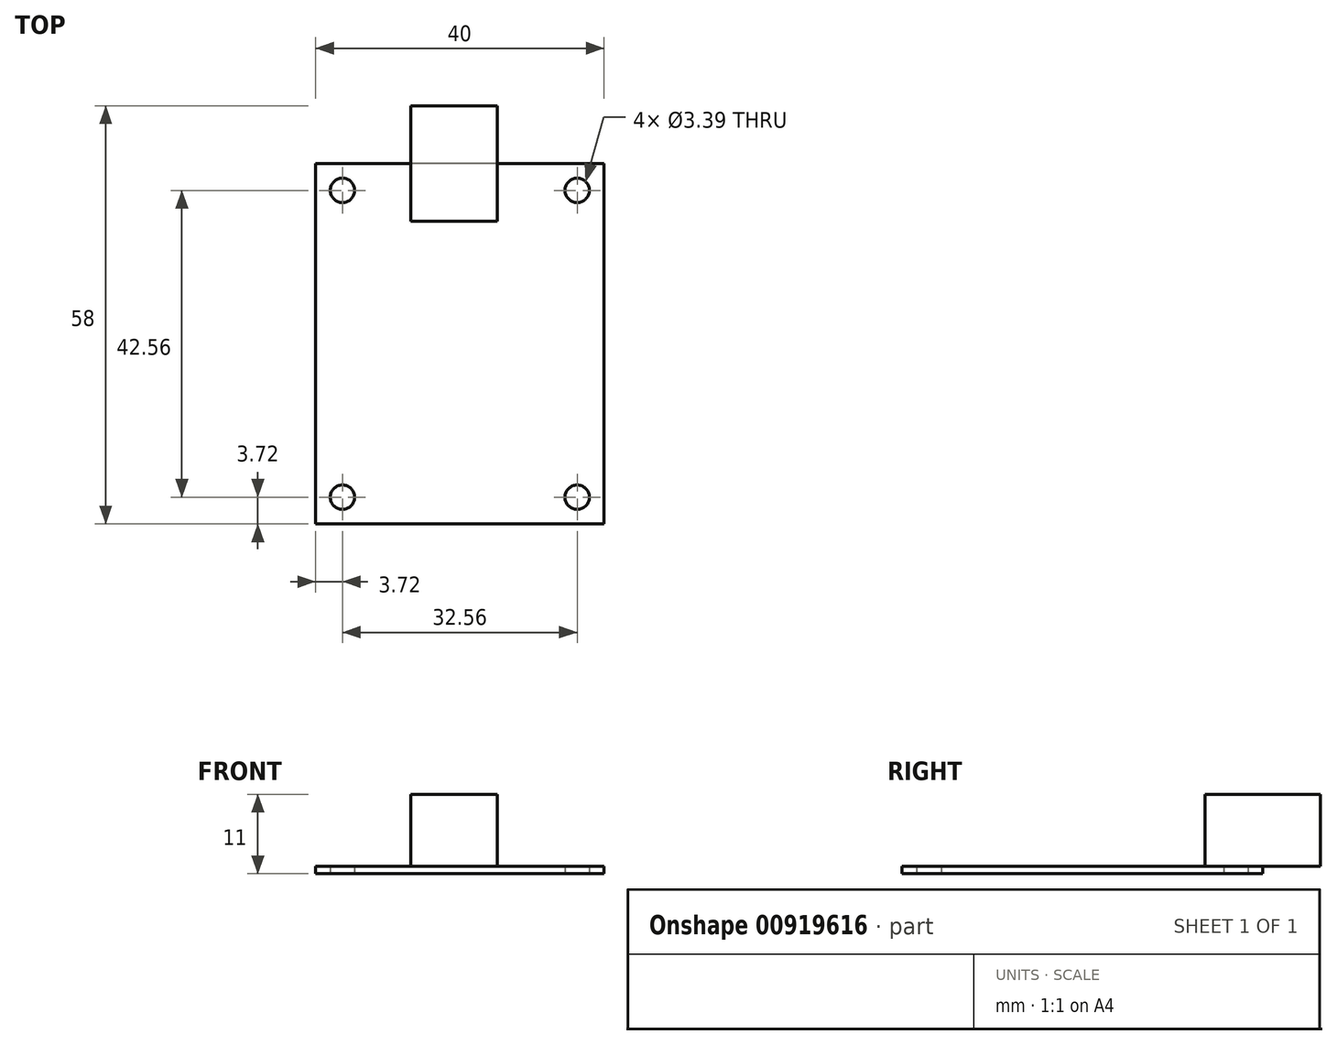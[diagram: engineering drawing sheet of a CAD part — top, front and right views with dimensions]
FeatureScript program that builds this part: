
annotation { "Feature Type Name" : "Feature", "Feature Type Description" : "" }
export const myFeature = defineFeature(function(context is Context, id is Id, definition is map)
    precondition{}
    {
        {
            var Q0;
            Q0=qCreatedBy(makeId("Top.planeOp"),FACE);
            var sketch = newSketch(context, id + "F0", { "sketchPlane" : qUnion([Q0])});
            skLineSegment(sketch, "E0.rect.bottom", {"start": v(20, -25) * mm, "end": v(-20, -25) * mm});
            skLineSegment(sketch, "E0.rect.top", {"start": v(20, 25) * mm, "end": v(-20, 25) * mm});
            skLineSegment(sketch, "E0.rect.left", {"start": v(20, -25) * mm, "end": v(20, 25) * mm});
            skLineSegment(sketch, "E0.rect.right", {"start": v(-20, -25) * mm, "end": v(-20, 25) * mm});
            skPoint(sketch, "E0.rect.middle", {"position": v(0, 0) * mm});
            skCircle(sketch, "E1", {"center": v(-16.28, 21.28) * mm, "radius": 1.7 * mm});
            skLineSegment(sketch, "E2", {"start": v(-26.55, 0) * mm, "end": v(31.37, 0) * mm, "construction": true});
            skLineSegment(sketch, "E3", {"start": v(0, -34.94) * mm, "end": v(0, 31.45) * mm, "construction": true});
            skCircle(sketch, "E4.MirrorC", {"center": v(16.28, 21.28) * mm, "radius": 1.7 * mm});
            skCircle(sketch, "E5.MirrorC", {"center": v(-16.28, -21.28) * mm, "radius": 1.7 * mm});
            skCircle(sketch, "E6.MirrorC", {"center": v(16.28, -21.28) * mm, "radius": 1.7 * mm});
            skSolve(sketch);
        }
        {
            var Q0;
            Q0=qSketchRegion(id+"F0",true);
            extrude(context, id + "F1", {"entities" : qUnion([Q0]), "depth" : 1 * mm});
        }
        {
            var Q0;
            Q0=makeQuery(id+"F1.opExtrude","CAP_FACE",FACE,{"disambiguationData":[OSD([sQuery(id+"F0.wireOp",EDGE,"E0.rect.bottom"),sQuery(id+"F0.wireOp",EDGE,"E0.rect.top"),sQuery(id+"F0.wireOp",EDGE,"E0.rect.left"),sQuery(id+"F0.wireOp",EDGE,"E0.rect.right"),sQuery(id+"F0.wireOp",EDGE,"E1"),sQuery(id+"F0.wireOp",EDGE,"E4.MirrorC"),sQuery(id+"F0.wireOp",EDGE,"E5.MirrorC"),sQuery(id+"F0.wireOp",EDGE,"E6.MirrorC")])],"isStart":false});
            var sketch = newSketch(context, id + "F2", { "sketchPlane" : qUnion([Q0])});
            skLineSegment(sketch, "E7.bottom", {"start": v(-6.83, 33) * mm, "end": v(5.17, 33) * mm});
            skLineSegment(sketch, "E7.top", {"start": v(-6.83, 17) * mm, "end": v(5.17, 17) * mm});
            skLineSegment(sketch, "E7.left", {"start": v(-6.83, 33) * mm, "end": v(-6.83, 17) * mm});
            skLineSegment(sketch, "E7.right", {"start": v(5.17, 33) * mm, "end": v(5.17, 17) * mm});
            skSolve(sketch);
        }
        {
            var Q0;
            Q0=qSketchRegion(id+"F2",true);
            extrude(context, id + "F3", {"entities" : qUnion([Q0]), "operationType" : NewBodyOperationType.ADD, "depth" : 10 * mm});
        }
    });
